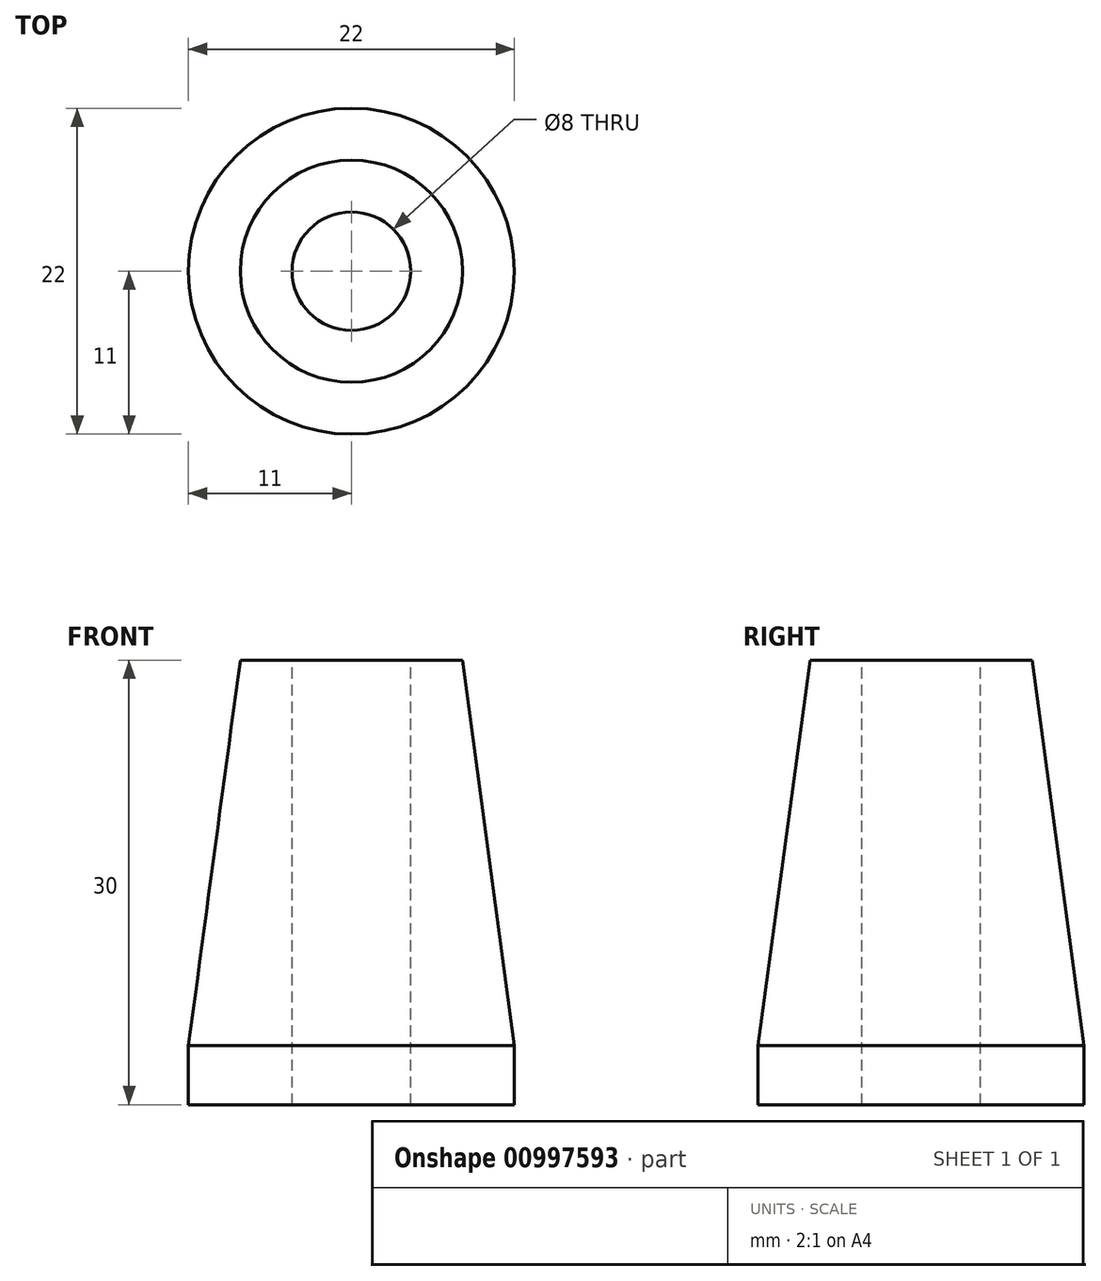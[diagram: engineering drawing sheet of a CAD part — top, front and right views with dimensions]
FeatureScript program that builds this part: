
annotation { "Feature Type Name" : "Feature", "Feature Type Description" : "" }
export const myFeature = defineFeature(function(context is Context, id is Id, definition is map)
    precondition{}
    {
        {
            var Q0;
            Q0=qCreatedBy(makeId("Right.planeOp"),FACE);
            var sketch = newSketch(context, id + "F0", { "sketchPlane" : qUnion([Q0])});
            skLineSegment(sketch, "E0", {"start": v(0, 0) * mm, "end": v(0, 30) * mm});
            skLineSegment(sketch, "E1", {"start": v(0, 0) * mm, "end": v(-11, 0) * mm});
            skLineSegment(sketch, "E2", {"start": v(-11, 0) * mm, "end": v(-11, 4) * mm});
            skLineSegment(sketch, "E3", {"start": v(0, 30) * mm, "end": v(-7.5, 30) * mm});
            skLineSegment(sketch, "E4", {"start": v(-7.5, 30) * mm, "end": v(-11, 4) * mm});
            skSolve(sketch);
        }
        {
            var Q0;
            Q0=makeQuery(id+"F0.imprint","IMPRINT",FACE,{"disambiguationData":[TD([[makeQuery(id+"F0.imprint","IMPRINT",EDGE,{"derivedFrom":sQuery(id+"F0.wireOp",EDGE,"E0")}),1.0]])]});
            var Q1;
            Q1=sQuery(id+"F0.wireOp",EDGE,"E0");
            revolve(context, id + "F1", {"surfaceOperationType" : NewSurfaceOperationType.NEW, "entities" : qUnion([Q0]), "axis" : qUnion([Q1]), "revolveType" : RevolveType.FULL});
        }
        {
            var Q0;
            Q0=makeQuery(id+"F1.opRevolve","SWEPT_FACE",FACE,{"disambiguationData":[OSD([sQuery(id+"F0.wireOp",EDGE,"E3")])]});
            var sketch = newSketch(context, id + "F2", { "sketchPlane" : qUnion([Q0])});
            skCircle(sketch, "E5", {"center": v(0, 0) * mm, "radius": 4 * mm});
            skSolve(sketch);
        }
        {
            var Q0;
            Q0=makeQuery(id+"F2.imprint","IMPRINT",FACE,{"disambiguationData":[TD([[makeQuery(id+"F2.imprint","IMPRINT",EDGE,{"derivedFrom":sQuery(id+"F2.wireOp",EDGE,"E5")}),1.0]])]});
            extrude(context, id + "F3", {"entities" : qUnion([Q0]), "operationType" : NewBodyOperationType.REMOVE, "oppositeDirection" : true, "depth" : 30 * mm, "offsetDistance" : 25 * mm});
        }
    });
